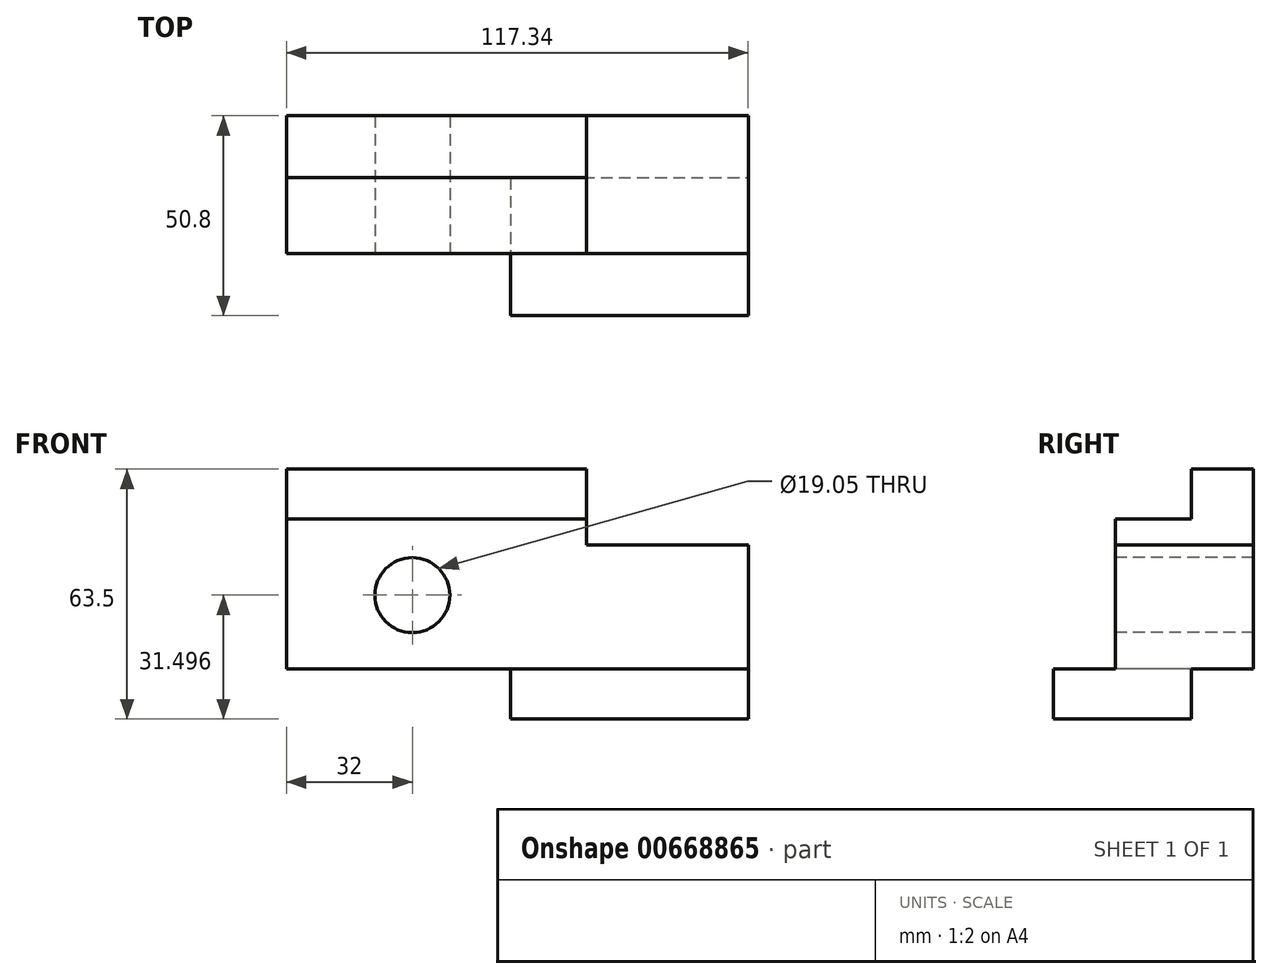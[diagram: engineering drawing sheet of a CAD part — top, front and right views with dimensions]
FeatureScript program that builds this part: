
annotation { "Feature Type Name" : "Feature", "Feature Type Description" : "" }
export const myFeature = defineFeature(function(context is Context, id is Id, definition is map)
    precondition{}
    {
        {
            var Q0;
            Q0=qCreatedBy(makeId("Front.planeOp"),FACE);
            var sketch = newSketch(context, id + "F0", { "sketchPlane" : qUnion([Q0])});
            skLineSegment(sketch, "E0.bottom", {"start": v(58.67, 31.75) * mm, "end": v(-58.67, 31.75) * mm});
            skLineSegment(sketch, "E0.top", {"start": v(58.67, -31.75) * mm, "end": v(-58.67, -31.75) * mm});
            skLineSegment(sketch, "E0.left", {"start": v(58.67, 31.75) * mm, "end": v(58.67, -31.75) * mm});
            skLineSegment(sketch, "E0.right", {"start": v(-58.67, 31.75) * mm, "end": v(-58.67, -31.75) * mm});
            skPoint(sketch, "E0.middle", {"position": v(0, 0) * mm});
            skSolve(sketch);
        }
        {
            var Q0;
            Q0 = qSketchRegion(id + "F0", true);
            extrude(context, id + "F1", {"entities" : qUnion([Q0]), "depth" : 50.8 * mm, "offsetDistance" : 25.4 * mm});
        }
        {
            var Q0;
            Q0=makeQuery(id+"F1.opExtrude","CAP_FACE",FACE,{"disambiguationData":[OSD([sQuery(id+"F0.wireOp",EDGE,"E0.bottom"),sQuery(id+"F0.wireOp",EDGE,"E0.top"),sQuery(id+"F0.wireOp",EDGE,"E0.left"),sQuery(id+"F0.wireOp",EDGE,"E0.right")])],"isStart":false});
            var sketch = newSketch(context, id + "F2", { "sketchPlane" : qUnion([Q0])});
            skLineSegment(sketch, "E1.bottom", {"start": v(58.67, 31.75) * mm, "end": v(17.53, 31.75) * mm});
            skLineSegment(sketch, "E1.top", {"start": v(58.67, 12.45) * mm, "end": v(17.53, 12.45) * mm});
            skLineSegment(sketch, "E1.left", {"start": v(58.67, 31.75) * mm, "end": v(58.67, 12.45) * mm});
            skLineSegment(sketch, "E1.right", {"start": v(17.53, 31.75) * mm, "end": v(17.53, 12.45) * mm});
            skSolve(sketch);
        }
        {
            var Q0;
            Q0 = qSketchRegion(id + "F2", true);
            extrude(context, id + "F3", {"entities" : qUnion([Q0]), "operationType" : NewBodyOperationType.REMOVE, "endBound" : BoundingType.THROUGH_ALL, "oppositeDirection" : true, "depth" : 25.4 * mm, "offsetDistance" : 25.4 * mm});
        }
        {
            var Q0;
            Q0=makeQuery(id+"F1.opExtrude","CAP_FACE",FACE,{"disambiguationData":[OSD([sQuery(id+"F0.wireOp",EDGE,"E0.bottom"),sQuery(id+"F0.wireOp",EDGE,"E0.top"),sQuery(id+"F0.wireOp",EDGE,"E0.left"),sQuery(id+"F0.wireOp",EDGE,"E0.right")])],"isStart":false});
            var sketch = newSketch(context, id + "F4", { "sketchPlane" : qUnion([Q0])});
            skLineSegment(sketch, "E2.bottom", {"start": v(-58.67, -31.75) * mm, "end": v(-1.78, -31.75) * mm});
            skLineSegment(sketch, "E2.top", {"start": v(-58.67, -19.05) * mm, "end": v(-1.78, -19.05) * mm});
            skLineSegment(sketch, "E2.left", {"start": v(-58.67, -31.75) * mm, "end": v(-58.67, -19.05) * mm});
            skLineSegment(sketch, "E2.right", {"start": v(-1.78, -31.75) * mm, "end": v(-1.78, -19.05) * mm});
            skSolve(sketch);
        }
        {
            var Q0;
            Q0 = qSketchRegion(id + "F4", true);
            extrude(context, id + "F5", {"entities" : qUnion([Q0]), "operationType" : NewBodyOperationType.REMOVE, "endBound" : BoundingType.THROUGH_ALL, "oppositeDirection" : true, "depth" : 25.4 * mm, "offsetDistance" : 25.4 * mm});
        }
        {
            var Q0;
            Q0=makeQuery(id+"F1.opExtrude","CAP_FACE",FACE,{"disambiguationData":[OSD([sQuery(id+"F0.wireOp",EDGE,"E0.bottom"),sQuery(id+"F0.wireOp",EDGE,"E0.top"),sQuery(id+"F0.wireOp",EDGE,"E0.left"),sQuery(id+"F0.wireOp",EDGE,"E0.right")])],"isStart":false});
            var sketch = newSketch(context, id + "F6", { "sketchPlane" : qUnion([Q0])});
            skCircle(sketch, "E3", {"center": v(-26.67, -0.25) * mm, "radius": 9.53 * mm});
            skSolve(sketch);
        }
        {
            var Q0;
            Q0 = qSketchRegion(id + "F6", true);
            extrude(context, id + "F7", {"entities" : qUnion([Q0]), "operationType" : NewBodyOperationType.REMOVE, "endBound" : BoundingType.THROUGH_ALL, "oppositeDirection" : true, "depth" : 25.4 * mm, "offsetDistance" : 25.4 * mm});
        }
        {
            var Q0;
            Q0=makeQuery(id+"F1.opExtrude","SWEPT_FACE",FACE,{"disambiguationData":[OSD([sQuery(id+"F0.wireOp",EDGE,"E0.left")])]});
            var sketch = newSketch(context, id + "F8", { "sketchPlane" : qUnion([Q0])});
            skLineSegment(sketch, "E4.bottom", {"start": v(0, -31.75) * mm, "end": v(-15.75, -31.75) * mm});
            skLineSegment(sketch, "E4.top", {"start": v(0, -19.05) * mm, "end": v(-15.75, -19.05) * mm});
            skLineSegment(sketch, "E4.left", {"start": v(0, -31.75) * mm, "end": v(0, -19.05) * mm});
            skLineSegment(sketch, "E4.right", {"start": v(-15.75, -31.75) * mm, "end": v(-15.75, -19.05) * mm});
            skSolve(sketch);
        }
        {
            var Q0;
            Q0 = qSketchRegion(id + "F8", true);
            extrude(context, id + "F9", {"entities" : qUnion([Q0]), "operationType" : NewBodyOperationType.REMOVE, "endBound" : BoundingType.THROUGH_ALL, "oppositeDirection" : true, "depth" : 25.4 * mm, "offsetDistance" : 25.4 * mm});
        }
        {
            var Q0;
            Q0=makeQuery(id+"F3.boolean.opBoolean","COPY",FACE,{"derivedFrom":makeQuery(id+"F3.opExtrude","SWEPT_FACE",FACE,{"disambiguationData":[OSD([sQuery(id+"F2.wireOp",EDGE,"E1.right")])]})});
            var sketch = newSketch(context, id + "F10", { "sketchPlane" : qUnion([Q0])});
            skLineSegment(sketch, "E5.bottom", {"start": v(-50.8, 31.75) * mm, "end": v(-15.75, 31.75) * mm});
            skLineSegment(sketch, "E5.top", {"start": v(-50.8, 19.05) * mm, "end": v(-15.75, 19.05) * mm});
            skLineSegment(sketch, "E5.left", {"start": v(-50.8, 31.75) * mm, "end": v(-50.8, 19.05) * mm});
            skLineSegment(sketch, "E5.right", {"start": v(-15.75, 31.75) * mm, "end": v(-15.75, 19.05) * mm});
            skSolve(sketch);
        }
        {
            var Q0;
            Q0 = qSketchRegion(id + "F10", true);
            extrude(context, id + "F11", {"entities" : qUnion([Q0]), "operationType" : NewBodyOperationType.REMOVE, "endBound" : BoundingType.THROUGH_ALL, "oppositeDirection" : true, "depth" : 25.4 * mm, "offsetDistance" : 25.4 * mm});
        }
        {
            var Q0;
            Q0=makeQuery(id+"F3.boolean.opBoolean","COPY",FACE,{"derivedFrom":makeQuery(id+"F3.opExtrude","SWEPT_FACE",FACE,{"disambiguationData":[OSD([sQuery(id+"F2.wireOp",EDGE,"E1.right")])]})});
            var sketch = newSketch(context, id + "F12", { "sketchPlane" : qUnion([Q0])});
            skLineSegment(sketch, "E6.bottom", {"start": v(-50.8, 19.05) * mm, "end": v(-35.05, 19.05) * mm});
            skLineSegment(sketch, "E6.top", {"start": v(-50.8, -19.05) * mm, "end": v(-35.05, -19.05) * mm});
            skLineSegment(sketch, "E6.left", {"start": v(-50.8, 19.05) * mm, "end": v(-50.8, -19.05) * mm});
            skLineSegment(sketch, "E6.right", {"start": v(-35.05, 19.05) * mm, "end": v(-35.05, -19.05) * mm});
            skSolve(sketch);
        }
        {
            var Q0;
            Q0 = qSketchRegion(id + "F12", true);
            extrude(context, id + "F13", {"entities" : qUnion([Q0]), "operationType" : NewBodyOperationType.REMOVE, "endBound" : BoundingType.THROUGH_ALL, "oppositeDirection" : true, "depth" : 25.4 * mm, "offsetDistance" : 25.4 * mm});
        }
        {
            var Q0;
            Q0=makeQuery(id+"F1.opExtrude","SWEPT_FACE",FACE,{"disambiguationData":[OSD([sQuery(id+"F0.wireOp",EDGE,"E0.left")])]});
            var sketch = newSketch(context, id + "F14", { "sketchPlane" : qUnion([Q0])});
            skLineSegment(sketch, "E7.bottom", {"start": v(-50.8, 12.45) * mm, "end": v(-35.05, 12.45) * mm});
            skLineSegment(sketch, "E7.top", {"start": v(-50.8, -19.05) * mm, "end": v(-35.05, -19.05) * mm});
            skLineSegment(sketch, "E7.left", {"start": v(-50.8, 12.45) * mm, "end": v(-50.8, -19.05) * mm});
            skLineSegment(sketch, "E7.right", {"start": v(-35.05, 12.45) * mm, "end": v(-35.05, -19.05) * mm});
            skSolve(sketch);
        }
        {
            var Q0;
            Q0 = qSketchRegion(id + "F14", true);
            extrude(context, id + "F15", {"entities" : qUnion([Q0]), "operationType" : NewBodyOperationType.REMOVE, "endBound" : BoundingType.THROUGH_ALL, "oppositeDirection" : true, "depth" : 25.4 * mm, "offsetDistance" : 25.4 * mm});
        }
    });
